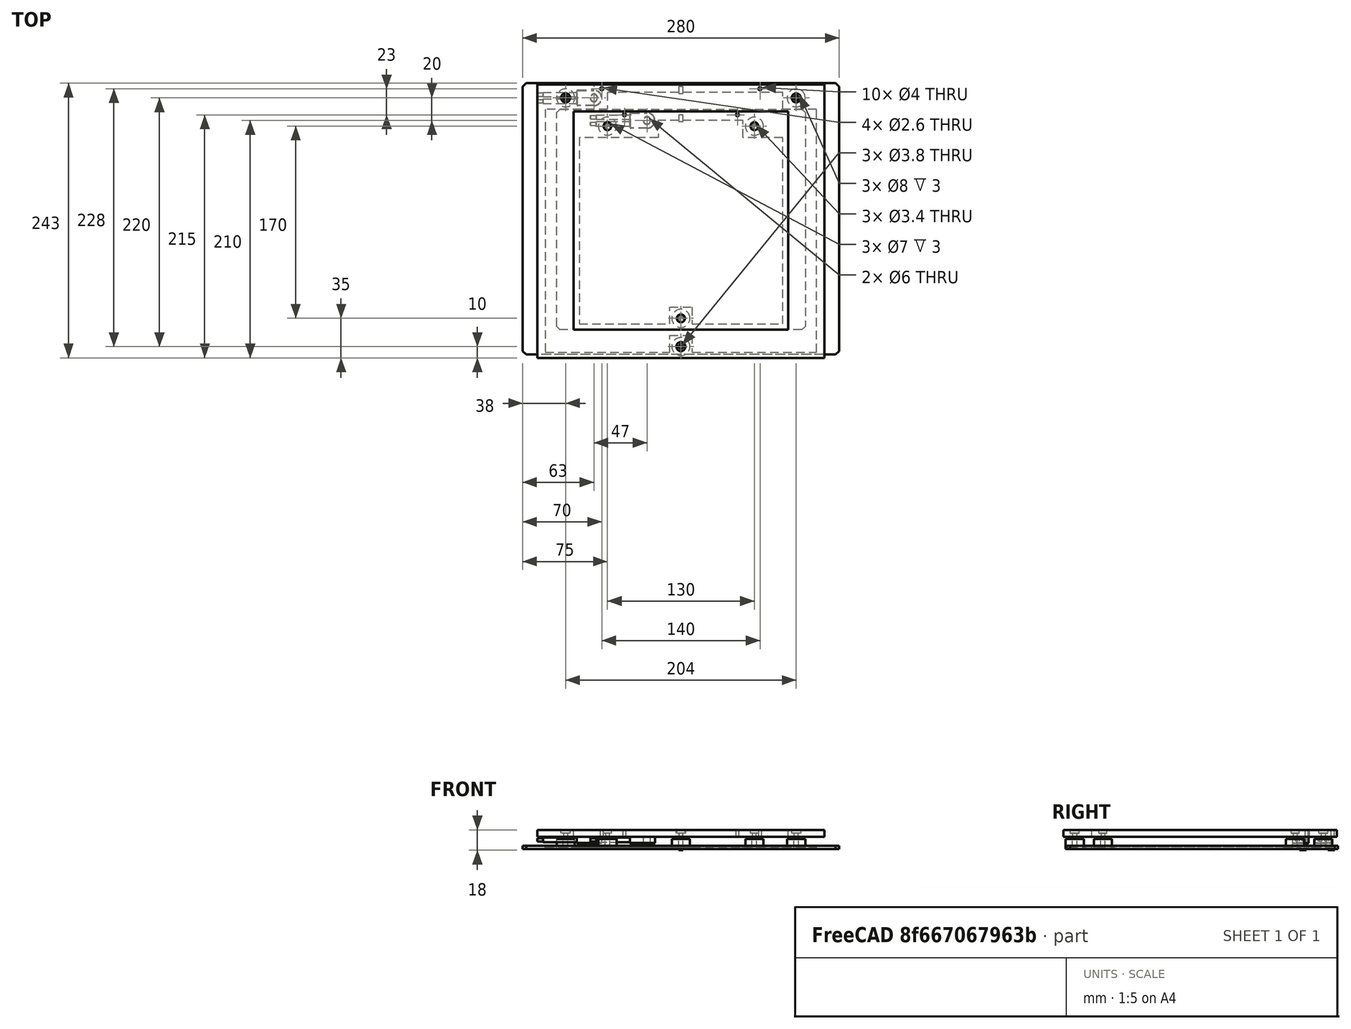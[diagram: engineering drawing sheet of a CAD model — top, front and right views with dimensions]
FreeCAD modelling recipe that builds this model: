
FCSTD DOCUMENT  (FreeCAD 0.19R24291 (Git))
Label: aluminum-bed
License: Other
LicenseURL: GPL3
objects: TechDraw::DrawViewDimension×50, Sketcher::SketchObject×10, TechDraw::DrawViewAnnotation×9, PartDesign::Pad×8, Part::Feature×8, PartDesign::Body×6, TechDraw::DrawSVGTemplate×5, TechDraw::DrawViewPart×5, TechDraw::DrawPage×5, TechDraw::DrawViewBalloon×3, PartDesign::Pocket×2, TechDraw::DrawViewSection×2, App::Part×2, PartDesign::Chamfer×2, TechDraw::DrawViewImage×1
note: 48 computed .brp shape members not serialized (recipe doc carries the construction recipe); baked Part::Feature solids carry a one-line shape summary decoded from their .brp

FEATURE [Sketcher::SketchObject] Sketch
  FullyConstrained = true
  MapMode = 5
  Support = -> [XY_Plane]
  sketch-geometry (9):
    g0: LineSegment StartX=-95 StartY=98 StartZ=0 EndX=95 EndY=98 EndZ=0
    g1: LineSegment StartX=95 StartY=98 StartZ=0 EndX=95 EndY=-95 EndZ=0
    g2: LineSegment StartX=95 StartY=-95 StartZ=0 EndX=-95 EndY=-95 EndZ=0
    g3: LineSegment StartX=-95 StartY=-95 StartZ=0 EndX=-95 EndY=98 EndZ=0
    g4: Circle CenterX=-1.4e-15 CenterY=-85 CenterZ=0 NormalX=0 NormalY=0 NormalZ=1 AngleXU=0 Radius=1.7
    g5: Circle CenterX=-65 CenterY=85 CenterZ=0 NormalX=0 NormalY=0 NormalZ=1 AngleXU=0 Radius=1.7
    g6: Circle CenterX=65 CenterY=85 CenterZ=0 NormalX=0 NormalY=0 NormalZ=1 AngleXU=0 Radius=1.7
    g7: Circle CenterX=-50 CenterY=95 CenterZ=0 NormalX=0 NormalY=0 NormalZ=1 AngleXU=0 Radius=1.3
    g8: Circle CenterX=50 CenterY=95 CenterZ=0 NormalX=0 NormalY=0 NormalZ=1 AngleXU=0 Radius=1.3
  constraints (27):
    c: Coincident(g0,g1)
    c: Coincident(g1,g2)
    c: Coincident(g2,g3)
    c: Coincident(g3,g0)
    c: Horizontal(g0)
    c: Horizontal(g2)
    c: Vertical(g1)
    c: Vertical(g3)
    c: DistanceY(g1,g1) = 193
    c: DistanceY(g2,g-1) = 95
    c: DistanceX(g0,g0) = 190
    c: DistanceX(g0,g-1) = 95
    c: DistanceX(g2,g4) = 95
    c: DistanceY(g1,g4) = 10
    c: DistanceY(g5,g0) = 13
    c: DistanceY(g6,g0) = 13
    c: DistanceX(g0,g5) = 30
    c: DistanceX(g6,g0) = 30
    c: Radius(g5) = 1.7
    c: Radius(g6) = 1.7
    c: Radius(g4) = 1.7
    c: DistanceX(g8,g0) = 45
    c: DistanceX(g0,g7) = 45
    c: Radius(g7) = 1.3
    c: Radius(g8) = 1.3
    c: DistanceY(g7,g0) = 3
    c: DistanceY(g8,g0) = 3
FEATURE [PartDesign::Pad] Pad
  Direction = (1,1,1)
  Length = 6
  Length2 = 100
  Profile = -> Sketch
  Type = 0
FEATURE [Sketcher::SketchObject] Sketch001
  FullyConstrained = true
  MapMode = 5
  Placement = pos=(0,0,6) rot=(0,0,1;0rad)
  Support = -> [Pad]
  sketch-geometry (3):
    g0: Circle CenterX=-65 CenterY=85 CenterZ=0 NormalX=0 NormalY=0 NormalZ=1 AngleXU=0 Radius=3.5
    g1: Circle CenterX=65 CenterY=85 CenterZ=0 NormalX=0 NormalY=0 NormalZ=1 AngleXU=0 Radius=3.5
    g2: Circle CenterX=0 CenterY=-85 CenterZ=0 NormalX=0 NormalY=0 NormalZ=1 AngleXU=0 Radius=3.5
  constraints (9):
    c: PointOnObject(g2,g-2)
    c: DistanceX(g0,g-1) = 65
    c: DistanceX(g-1,g1) = 65
    c: DistanceY(g2,g-1) = 85
    c: DistanceY(g-1,g0) = 85
    c: DistanceY(g-1,g1) = 85
    c: Radius(g0) = 3.5
    c: Radius(g1) = 3.5
    c: Radius(g2) = 3.5
FEATURE [PartDesign::Pocket] Pocket
  BaseFeature = -> Pad
  Length = 3
  Length2 = 100
  Profile = -> Sketch001
  Type = 0
FEATURE [PartDesign::Body] Body  label="190x193mm-bed"
  Group = -> [Sketch,Pad,Sketch001,Pocket]
  Origin = -> Origin
  Placement = pos=(0,0,11) rot=(0,0,1;0rad)
  Tip = -> Pocket
FEATURE [Sketcher::SketchObject] Sketch002
  FullyConstrained = true
  MapMode = 5
  Support = -> [XY_Plane001]
  sketch-geometry (9):
    g0: LineSegment StartX=-127 StartY=122 StartZ=0 EndX=127 EndY=122 EndZ=0
    g1: LineSegment StartX=127 StartY=122 StartZ=0 EndX=127 EndY=-120 EndZ=0
    g2: LineSegment StartX=127 StartY=-120 StartZ=0 EndX=-127 EndY=-120 EndZ=0
    g3: LineSegment StartX=-127 StartY=-120 StartZ=0 EndX=-127 EndY=122 EndZ=0
    g4: Circle CenterX=-102 CenterY=110 CenterZ=0 NormalX=0 NormalY=0 NormalZ=1 AngleXU=0 Radius=1.9
    g5: Circle CenterX=102 CenterY=110 CenterZ=0 NormalX=0 NormalY=0 NormalZ=1 AngleXU=0 Radius=1.9
    g6: Circle CenterX=0 CenterY=-110 CenterZ=0 NormalX=0 NormalY=0 NormalZ=1 AngleXU=0 Radius=1.9
    g7: Circle CenterX=-70 CenterY=118 CenterZ=0 NormalX=0 NormalY=0 NormalZ=1 AngleXU=0 Radius=1.3
    g8: Circle CenterX=70 CenterY=118 CenterZ=0 NormalX=0 NormalY=0 NormalZ=1 AngleXU=0 Radius=1.3
  constraints (27):
    c: Coincident(g0,g1)
    c: Coincident(g1,g2)
    c: Coincident(g2,g3)
    c: Coincident(g3,g0)
    c: Horizontal(g0)
    c: Horizontal(g2)
    c: Vertical(g1)
    c: Vertical(g3)
    c: DistanceX(g2,g2) = 254
    c: DistanceX(g2,g-1) = 127
    c: DistanceY(g3,g3) = 242
    c: DistanceY(g-1,g0) = 122
    c: DistanceX(g0,g4) = 25
    c: DistanceX(g5,g0) = 25
    c: DistanceY(g4,g0) = 12
    c: DistanceY(g5,g0) = 12
    c: DistanceY(g1,g6) = 10
    c: DistanceX(g6,g-1) = 0
    c: DistanceX(g7,g8) = 140
    c: DistanceX(g7,g-1) = 70
    c: DistanceY(g7,g8) = 0
    c: Radius(g7) = 1.3
    c: Radius(g8) = 1.3
    c: DistanceY(g7,g0) = 4
    c: Radius(g4) = 1.9
    c: Radius(g5) = 1.9
    c: Radius(g6) = 1.9
FEATURE [PartDesign::Pad] Pad001
  Direction = (1,1,1)
  Length = 6
  Length2 = 100
  Profile = -> Sketch002
  Type = 0
FEATURE [Sketcher::SketchObject] Sketch003
  FullyConstrained = true
  MapMode = 5
  Placement = pos=(0,0,6) rot=(0,0,1;0rad)
  Support = -> [Pad001]
  sketch-geometry (3):
    g0: Circle CenterX=-102 CenterY=110 CenterZ=0 NormalX=0 NormalY=0 NormalZ=1 AngleXU=0 Radius=4
    g1: Circle CenterX=102 CenterY=110 CenterZ=0 NormalX=0 NormalY=0 NormalZ=1 AngleXU=0 Radius=4
    g2: Circle CenterX=0 CenterY=-110 CenterZ=0 NormalX=0 NormalY=0 NormalZ=1 AngleXU=0 Radius=4
  constraints (9):
    c: PointOnObject(g2,g-2)
    c: Radius(g2) = 4
    c: Radius(g0) = 4
    c: Radius(g1) = 4
    c: DistanceY(g-1,g1) = 110
    c: DistanceX(g-1,g1) = 102
    c: DistanceX(g0,g-1) = 102
    c: DistanceY(g0,g1) = 0
    c: DistanceY(g2,g-1) = 110
FEATURE [PartDesign::Pocket] Pocket001
  BaseFeature = -> Pad001
  Length = 3
  Length2 = 100
  Profile = -> Sketch003
  Type = 0
FEATURE [PartDesign::Body] Body001  label="254x240-bed"
  Group = -> [Sketch002,Pad001,Sketch003,Pocket001]
  Origin = -> Origin001
  Placement = pos=(0,0,11) rot=(0,0,1;0rad)
  Tip = -> Pocket001
FEATURE [TechDraw::DrawSVGTemplate] Template
  EditableTexts = APPROVER_NAME=CB; AUTHOR_NAME=SnakeOil XY; DATE=2021-11-11; DN=DN; DOCUMENT_TYPE=Mechanical assembly drawing; OWNER_NAME=SnakeOil XY; PM=Silicon heater; PN=SO-180Heater; REVISION=REV B; RIGHTS=(R) DO NOT DUPLICATE THIS DRAWING TO THIRD PARTIES WITHOUT OWNER'S PERMISSION!; SCALE=1.0; SHEET=99 of 99; SIZE=A3; TITLELINE-1=SnakeOil XY; TITLELINE-2=180x180mm Silicon heater 120V 350-400W; TITLELINE-3=Dimensions in mm; TOLERANCE=+/- 0.2mm
  Height = 297
  Orientation = 1
  Width = 420
FEATURE [TechDraw::DrawSVGTemplate] Template002
  EditableTexts = APPROVER_NAME=CB; AUTHOR_NAME=SnakeOil XY; DATE=2021-11-09; DN=DN; DOCUMENT_TYPE=Mechanical assembly drawing; OWNER_NAME=SnakeOil XY; PM=Aluminum 6mm Plate; PN=SO-250Bed; REVISION=REV A; RIGHTS=(R) DO NOT DUPLICATE THIS DRAWING TO THIRD PARTIES WITHOUT OWNER'S PERMISSION!; SCALE=0.75; SHEET=99 of 99; SIZE=A3; TITLELINE-1=SnakeOil XY; TITLELINE-2=242x254mm Aluminium Bed; TITLELINE-3=Dimensions in mm; TOLERANCE=+/- 0.2mm
  Height = 297
  Orientation = 1
  Width = 420
FEATURE [TechDraw::DrawViewPart] View002  label="Top View"
  CoarseView = false
  Direction = (0,0,1)
  Focus = 100
  HardHidden = true
  IsoCount = 0
  IsoHidden = true
  IsoVisible = false
  LockPosition = false
  Perspective = false
  Rotation = 0
  Scale = 0.75
  ScaleType = 0
  SeamHidden = true
  SeamVisible = true
  SmoothHidden = false
  SmoothVisible = true
  Source = -> [Body001]
  X = 187.091
  XDirection = (1,0,0)
  Y = 157.532
FEATURE [TechDraw::DrawViewDimension] Dimension008
  Arbitrary = false
  ArbitraryTolerances = false
  EqualTolerance = true
  FormatSpec = %.2f
  FormatSpecOverTolerance = %+.2f
  FormatSpecUnderTolerance = %+.2f
  Inverted = false
  LockPosition = false
  MeasureType = 1
  OverTolerance = 0
  References2D = -> [View002]
  Rotation = 0
  ScaleType = 0
  TheoreticalExact = false
  Type = 2
  UnderTolerance = 0
  X = -129.591
  Y = 4.6265
FEATURE [TechDraw::DrawViewDimension] Dimension009
  Arbitrary = false
  ArbitraryTolerances = false
  EqualTolerance = true
  FormatSpec = %.2f
  FormatSpecOverTolerance = %+.2f
  FormatSpecUnderTolerance = %+.2f
  Inverted = false
  LockPosition = false
  MeasureType = 1
  OverTolerance = 0
  References2D = -> [View002]
  Rotation = 0
  ScaleType = 0
  TheoreticalExact = false
  Type = 1
  UnderTolerance = 0
  X = -3.77464
  Y = 114.946
FEATURE [TechDraw::DrawViewDimension] Dimension010
  Arbitrary = false
  ArbitraryTolerances = false
  EqualTolerance = true
  FormatSpec = %.2f
  FormatSpecOverTolerance = %+.2f
  FormatSpecUnderTolerance = %+.2f
  Inverted = false
  LockPosition = false
  MeasureType = 1
  OverTolerance = 0
  References2D = -> [View002]
  Rotation = 0
  ScaleType = 0
  TheoreticalExact = false
  Type = 1
  UnderTolerance = 0
  X = -85.9693
  Y = 105.298
FEATURE [TechDraw::DrawViewDimension] Dimension018
  Arbitrary = false
  ArbitraryTolerances = false
  EqualTolerance = true
  FormatSpec = %.2f
  FormatSpecOverTolerance = %+.2f
  FormatSpecUnderTolerance = %+.2f
  Inverted = false
  LockPosition = false
  MeasureType = 1
  OverTolerance = 0
  References2D = -> [View002]
  Rotation = 0
  ScaleType = 0
  TheoreticalExact = false
  Type = 1
  UnderTolerance = 0
  X = -48.5489
  Y = -96.978
FEATURE [TechDraw::DrawViewDimension] Dimension019
  Arbitrary = false
  ArbitraryTolerances = false
  EqualTolerance = true
  FormatSpec = %.2f
  FormatSpecOverTolerance = %+.2f
  FormatSpecUnderTolerance = %+.2f
  Inverted = false
  LockPosition = false
  MeasureType = 1
  OverTolerance = 0
  References2D = -> [View002]
  Rotation = 0
  ScaleType = 0
  TheoreticalExact = false
  Type = 2
  UnderTolerance = 0
  X = -107.541
  Y = -67.6889
FEATURE [TechDraw::DrawViewDimension] Dimension024
  Arbitrary = false
  ArbitraryTolerances = false
  EqualTolerance = true
  FormatSpec = 3x ⌀%.2f THRU ALL
  FormatSpecOverTolerance = %+.2f
  FormatSpecUnderTolerance = %+.2f
  Inverted = false
  LockPosition = false
  MeasureType = 1
  OverTolerance = 0
  References2D = -> [View002]
  Rotation = 0
  ScaleType = 0
  TheoreticalExact = false
  Type = 5
  UnderTolerance = 0
  X = 28.5305
  Y = -62.0287
FEATURE [TechDraw::DrawViewDimension] Dimension011
  Arbitrary = false
  ArbitraryTolerances = false
  EqualTolerance = true
  FormatSpec = %.2f
  FormatSpecOverTolerance = %+.2f
  FormatSpecUnderTolerance = %+.2f
  Inverted = false
  LockPosition = false
  MeasureType = 1
  OverTolerance = 0
  References2D = -> [View002]
  Rotation = 0
  ScaleType = 0
  TheoreticalExact = false
  Type = 1
  UnderTolerance = 0
  X = -64.1413
  Y = 105.194
FEATURE [TechDraw::DrawViewDimension] Dimension028
  Arbitrary = false
  ArbitraryTolerances = false
  EqualTolerance = true
  FormatSpec = %.2f
  FormatSpecOverTolerance = %+.2f
  FormatSpecUnderTolerance = %+.2f
  Inverted = false
  LockPosition = false
  MeasureType = 1
  OverTolerance = 0
  References2D = -> [View002]
  Rotation = 0
  ScaleType = 0
  TheoreticalExact = false
  Type = 2
  UnderTolerance = 0
  X = -108.367
  Y = 69.0185
FEATURE [TechDraw::DrawViewSection] SectionView  label="Section A - A"
  BaseView = -> View002
  CoarseView = false
  CutSurfaceDisplay = 2
  Direction = (1,0,0)
  FileGeomPattern = C:/Program Files/FreeCAD 0.19/data/Mod/TechDraw/PAT/FCPAT.pat
  FileHatchPattern = C:/Program Files/FreeCAD 0.19/data/Mod/TechDraw/Patterns/simple.svg
  Focus = 100
  FuseBeforeCut = false
  HardHidden = true
  HatchScale = 1
  IsoCount = 0
  IsoHidden = false
  IsoVisible = false
  LockPosition = false
  NameGeomPattern = Diamond
  Perspective = false
  Rotation = 0
  Scale = 0.75
  ScaleType = 0
  SeamHidden = false
  SeamVisible = true
  SectionDirection = 1
  SectionNormal = (1,0,0)
  SectionOrigin = (0,1,-20)
  SectionSymbol = A
  SmoothHidden = false
  SmoothVisible = true
  Source = -> [Body001]
  X = 361.828
  XDirection = (0,0,-1)
  Y = 157.254
FEATURE [TechDraw::DrawViewDimension] Dimension030
  Arbitrary = false
  ArbitraryTolerances = false
  EqualTolerance = true
  FormatSpec = %.2f
  FormatSpecOverTolerance = %+.2f
  FormatSpecUnderTolerance = %+.2f
  Inverted = false
  LockPosition = false
  MeasureType = 1
  OverTolerance = 0
  References2D = -> [SectionView]
  Rotation = 0
  ScaleType = 0
  TheoreticalExact = false
  Type = 2
  UnderTolerance = 0
  X = -21.0566
  Y = -66.6227
FEATURE [TechDraw::DrawViewDimension] Dimension031
  Arbitrary = false
  ArbitraryTolerances = false
  EqualTolerance = true
  FormatSpec = %.2f
  FormatSpecOverTolerance = %+.2f
  FormatSpecUnderTolerance = %+.2f
  Inverted = false
  LockPosition = false
  MeasureType = 1
  OverTolerance = 0
  References2D = -> [SectionView]
  Rotation = 0
  ScaleType = 0
  TheoreticalExact = false
  Type = 0
  UnderTolerance = 0
  X = 11.4648
  Y = -70.64
FEATURE [TechDraw::DrawViewDimension] Dimension032
  Arbitrary = false
  ArbitraryTolerances = false
  EqualTolerance = true
  FormatSpec = %.2f
  FormatSpecOverTolerance = %+.2f
  FormatSpecUnderTolerance = %+.2f
  Inverted = false
  LockPosition = false
  MeasureType = 1
  OverTolerance = 0
  References2D = -> [SectionView]
  Rotation = 0
  ScaleType = 0
  TheoreticalExact = false
  Type = 0
  UnderTolerance = 0
  X = -2.15303
  Y = 102.385
FEATURE [TechDraw::DrawViewDimension] Dimension033
  Arbitrary = false
  ArbitraryTolerances = false
  EqualTolerance = true
  FormatSpec = %.2f
  FormatSpecOverTolerance = %+.2f
  FormatSpecUnderTolerance = %+.2f
  Inverted = false
  LockPosition = false
  MeasureType = 1
  OverTolerance = 0
  References2D = -> [View002]
  Rotation = 0
  ScaleType = 0
  TheoreticalExact = false
  Type = 2
  UnderTolerance = 0
  X = -117.954
  Y = 68.1477
FEATURE [TechDraw::DrawViewDimension] Dimension034
  Arbitrary = false
  ArbitraryTolerances = false
  EqualTolerance = true
  FormatSpec = 2x ⌀%.2f THRU ALL
  FormatSpecOverTolerance = %+.2f
  FormatSpecUnderTolerance = %+.2f
  Inverted = false
  LockPosition = false
  MeasureType = 1
  OverTolerance = 0
  References2D = -> [View002]
  Rotation = 0
  ScaleType = 0
  TheoreticalExact = false
  Type = 5
  UnderTolerance = 0
  X = 26.933
  Y = 78.1529
FEATURE [TechDraw::DrawViewImage] Image
  Height = 25
  ImageFile = <userpath>/Desktop/SnakeOil Logo Banner.png
  LockPosition = false
  Rotation = 0
  Scale = 0.12
  ScaleType = 2
  Width = 25
  X = 332.066
  Y = 27.4423
FEATURE [TechDraw::DrawViewAnnotation] Annotation
  Font = Open Sans
  LineSpace = 80
  LockPosition = false
  MaxWidth = -1
  Rotation = 0
  ScaleType = 0
  Text =  \u2334 \u23008.00 \u21a7 3.00
  TextSize = 5
  TextStyle = 0
  X = 211.577
  Y = 85.7344
FEATURE [TechDraw::DrawViewAnnotation] Annotation001
  Font = Open Sans
  LineSpace = 80
  LockPosition = false
  MaxWidth = -1
  Rotation = 0
  ScaleType = 0
  Text = M3 THRU ALL
  TextSize = 5
  TextStyle = 0
  X = 207.027
  Y = 225.227
FEATURE [TechDraw::DrawPage] Page002  label="250-aluminum-bed"
  KeepUpdated = true
  NextBalloonIndex = 3
  ProjectionType = 0
  Template = -> Template002
  Views = -> [View002,Dimension008,Dimension009,Dimension010,Dimension011,Dimension018,Dimension019,Dimension024,Dimension028,SectionView,Dimension030,Dimension031,Dimension032,Dimension033,Dimension034,Image,Annotation,Annotation001]
FEATURE [TechDraw::DrawSVGTemplate] Template003
  EditableTexts = APPROVER_NAME=CB; AUTHOR_NAME=SnakeOil XY; DATE=2021-11-09; DN=DN; DOCUMENT_TYPE=Mechanical assembly drawing; OWNER_NAME=SnakeOil XY; PM=Aluminum 6mm Plate; PN=SO-180Bed; REVISION=REV A; RIGHTS=(R) DO NOT DUPLICATE THIS DRAWING TO THIRD PARTIES WITHOUT OWNER'S PERMISSION!; SCALE=1.0; SHEET=99 of 99; SIZE=A3; TITLELINE-1=SnakeOil XY; TITLELINE-2=190x193mm Aluminium Bed; TITLELINE-3=Dimensions in mm; TOLERANCE=+/- 0.2mm
  Height = 297
  Orientation = 1
  Width = 420
FEATURE [TechDraw::DrawViewPart] View003
  CoarseView = false
  Direction = (0,0,1)
  Focus = 100
  HardHidden = true
  IsoCount = 0
  IsoHidden = true
  IsoVisible = false
  LockPosition = false
  Perspective = false
  Rotation = 0
  ScaleType = 0
  SeamHidden = true
  SeamVisible = true
  SmoothHidden = false
  SmoothVisible = true
  Source = -> [Body]
  X = 163.077
  XDirection = (1,0,0)
  Y = 159.843
FEATURE [TechDraw::DrawViewDimension] Dimension062
  Arbitrary = false
  ArbitraryTolerances = false
  EqualTolerance = true
  FormatSpec = %.2f
  FormatSpecOverTolerance = %+.2f
  FormatSpecUnderTolerance = %+.2f
  Inverted = false
  LockPosition = false
  MeasureType = 1
  OverTolerance = 0
  References2D = -> [View003]
  Rotation = 0
  ScaleType = 0
  TheoreticalExact = false
  Type = 2
  UnderTolerance = 0
  X = -125.383
  Y = 2.51695
FEATURE [TechDraw::DrawViewDimension] Dimension063
  Arbitrary = false
  ArbitraryTolerances = false
  EqualTolerance = true
  FormatSpec = %.2f
  FormatSpecOverTolerance = %+.2f
  FormatSpecUnderTolerance = %+.2f
  Inverted = false
  LockPosition = false
  MeasureType = 1
  OverTolerance = 0
  References2D = -> [View003]
  Rotation = 0
  ScaleType = 0
  TheoreticalExact = false
  Type = 2
  UnderTolerance = 0
  X = -116.496
  Y = 75.6174
FEATURE [TechDraw::DrawViewDimension] Dimension064
  Arbitrary = false
  ArbitraryTolerances = false
  EqualTolerance = true
  FormatSpec = %.2f
  FormatSpecOverTolerance = %+.2f
  FormatSpecUnderTolerance = %+.2f
  Inverted = false
  LockPosition = false
  MeasureType = 1
  OverTolerance = 0
  References2D = -> [View003]
  Rotation = 0
  ScaleType = 0
  TheoreticalExact = false
  Type = 2
  UnderTolerance = 0
  X = -107.25
  Y = 74.8161
FEATURE [TechDraw::DrawViewDimension] Dimension066
  Arbitrary = false
  ArbitraryTolerances = false
  EqualTolerance = true
  FormatSpec = %.2f
  FormatSpecOverTolerance = %+.2f
  FormatSpecUnderTolerance = %+.2f
  Inverted = false
  LockPosition = false
  MeasureType = 1
  OverTolerance = 0
  References2D = -> [View003]
  Rotation = 0
  ScaleType = 0
  TheoreticalExact = false
  Type = 1
  UnderTolerance = 0
  X = -47.3359
  Y = -97.9006
FEATURE [TechDraw::DrawViewDimension] Dimension067
  Arbitrary = false
  ArbitraryTolerances = false
  EqualTolerance = true
  FormatSpec = %.2f
  FormatSpecOverTolerance = %+.2f
  FormatSpecUnderTolerance = %+.2f
  Inverted = false
  LockPosition = false
  MeasureType = 1
  OverTolerance = 0
  References2D = -> [View003]
  Rotation = 0
  ScaleType = 0
  TheoreticalExact = false
  Type = 1
  UnderTolerance = 0
  X = -1.8053
  Y = 121.118
FEATURE [TechDraw::DrawViewDimension] Dimension068
  Arbitrary = false
  ArbitraryTolerances = false
  EqualTolerance = true
  FormatSpec = %.2f
  FormatSpecOverTolerance = %+.2f
  FormatSpecUnderTolerance = %+.2f
  Inverted = false
  LockPosition = false
  MeasureType = 1
  OverTolerance = 0
  References2D = -> [View003]
  Rotation = 0
  ScaleType = 0
  TheoreticalExact = false
  Type = 1
  UnderTolerance = 0
  X = -81.0404
  Y = 110.461
FEATURE [TechDraw::DrawViewDimension] Dimension069
  Arbitrary = false
  ArbitraryTolerances = false
  EqualTolerance = true
  FormatSpec = %.2f
  FormatSpecOverTolerance = %+.2f
  FormatSpecUnderTolerance = %+.2f
  Inverted = false
  LockPosition = false
  MeasureType = 1
  OverTolerance = 0
  References2D = -> [View003]
  Rotation = 0
  ScaleType = 0
  TheoreticalExact = false
  Type = 1
  UnderTolerance = 0
  X = -57.9335
  Y = 110.522
FEATURE [TechDraw::DrawViewDimension] Dimension070
  Arbitrary = false
  ArbitraryTolerances = false
  EqualTolerance = true
  FormatSpec = 2x ⌀%.2f THRU ALL
  FormatSpecOverTolerance = %+.2f
  FormatSpecUnderTolerance = %+.2f
  Inverted = false
  LockPosition = false
  MeasureType = 1
  OverTolerance = 0
  References2D = -> [View003]
  Rotation = 0
  ScaleType = 0
  TheoreticalExact = false
  Type = 5
  UnderTolerance = 0
  X = 23.3527
  Y = 89.8776
FEATURE [TechDraw::DrawViewDimension] Dimension071
  Arbitrary = false
  ArbitraryTolerances = false
  EqualTolerance = true
  FormatSpec = 3x ⌀%.2f THRU ALL
  FormatSpecOverTolerance = %+.2f
  FormatSpecUnderTolerance = %+.2f
  Inverted = false
  LockPosition = false
  MeasureType = 1
  OverTolerance = 0
  References2D = -> [View003]
  Rotation = 0
  ScaleType = 0
  TheoreticalExact = false
  Type = 5
  UnderTolerance = 0
  X = 33.3476
  Y = -62.6573
FEATURE [TechDraw::DrawViewAnnotation] Annotation002
  Font = osifont
  LineSpace = 80
  LockPosition = false
  MaxWidth = -1
  Rotation = 0
  ScaleType = 0
  Text = M3 THRU ALL
  TextSize = 5
  TextStyle = 0
  X = 180.845
  Y = 237.091
FEATURE [TechDraw::DrawViewAnnotation] Annotation003
  Font = osifont
  LineSpace = 80
  LockPosition = false
  MaxWidth = -1
  Rotation = 0
  ScaleType = 0
  Text =  \u2334 \u23007.00 \u21a7 3.00
  TextSize = 5
  TextStyle = 0
  X = 198.079
  Y = 84.8751
FEATURE [TechDraw::DrawViewSection] SectionView001  label="Section A - A001"
  BaseView = -> View003
  CoarseView = false
  CutSurfaceDisplay = 2
  Direction = (1,0,0)
  FileGeomPattern = <path>
  FileHatchPattern = <path>
  Focus = 100
  FuseBeforeCut = false
  HardHidden = false
  HatchScale = 1
  IsoCount = 0
  IsoHidden = false
  IsoVisible = false
  LockPosition = false
  NameGeomPattern = Diamond
  Perspective = false
  Rotation = 0
  ScaleType = 0
  SeamHidden = false
  SeamVisible = true
  SectionDirection = 1
  SectionNormal = (1,0,0)
  SectionOrigin = (0,1.5,-43)
  SectionSymbol = A
  SmoothHidden = false
  SmoothVisible = true
  Source = -> [Body]
  X = 321.285
  XDirection = (0,0,-1)
  Y = 159.826
FEATURE [TechDraw::DrawViewDimension] Dimension072
  Arbitrary = false
  ArbitraryTolerances = false
  EqualTolerance = true
  FormatSpec = %.2f
  FormatSpecOverTolerance = %+.2f
  FormatSpecUnderTolerance = %+.2f
  Inverted = false
  LockPosition = false
  MeasureType = 1
  OverTolerance = 0
  References2D = -> [SectionView001]
  Rotation = 0
  ScaleType = 0
  TheoreticalExact = false
  Type = 1
  UnderTolerance = 0
  X = -0.208081
  Y = 106.28
FEATURE [TechDraw::DrawViewDimension] Dimension073
  Arbitrary = false
  ArbitraryTolerances = false
  EqualTolerance = true
  FormatSpec = %.2f
  FormatSpecOverTolerance = %+.2f
  FormatSpecUnderTolerance = %+.2f
  Inverted = false
  LockPosition = false
  MeasureType = 1
  OverTolerance = 0
  References2D = -> [SectionView001]
  Rotation = 0
  ScaleType = 0
  TheoreticalExact = false
  Type = 2
  UnderTolerance = 0
  X = -20.3682
  Y = -75.6723
FEATURE [TechDraw::DrawViewDimension] Dimension074
  Arbitrary = false
  ArbitraryTolerances = false
  EqualTolerance = true
  FormatSpec = %.2f
  FormatSpecOverTolerance = %+.2f
  FormatSpecUnderTolerance = %+.2f
  Inverted = false
  LockPosition = false
  MeasureType = 1
  OverTolerance = 0
  References2D = -> [SectionView001]
  Rotation = 0
  ScaleType = 0
  TheoreticalExact = false
  Type = 1
  UnderTolerance = 0
  X = 9.43758
  Y = -71.1281
FEATURE [TechDraw::DrawViewDimension] Dimension075
  Arbitrary = false
  ArbitraryTolerances = false
  EqualTolerance = true
  FormatSpec = %.2f
  FormatSpecOverTolerance = %+.2f
  FormatSpecUnderTolerance = %+.2f
  Inverted = false
  LockPosition = false
  MeasureType = 1
  OverTolerance = 0
  References2D = -> [View003]
  Rotation = 0
  ScaleType = 0
  TheoreticalExact = false
  Type = 2
  UnderTolerance = 0
  X = -111.672
  Y = -73.2721
FEATURE [TechDraw::DrawPage] Page003  label="180-aluminum-bed"
  KeepUpdated = true
  NextBalloonIndex = 1
  ProjectionType = 0
  Template = -> Template003
  Views = -> [View003,Dimension062,Dimension063,Dimension064,Dimension066,Dimension067,Dimension068,Dimension069,Dimension070,Dimension071,Annotation002,Annotation003,SectionView001,Dimension072,Dimension073,Dimension074,Dimension075]
FEATURE [Part::Feature] Part__Feature003  label="thermal-fuse-180"
  Placement = pos=(-30,90,11.18) rot=(0,1,0;1.5708rad)
  shape: bbox 57 x 14 x 6 mm, 31 faces (baked)
FEATURE [Part::Feature] Cut001  label="silicon-spacer"
  Placement = pos=(65,85,0) rot=(0,0,1;0rad)
  shape: bbox 16 x 16 x 9 mm, 4 faces (baked)
FEATURE [Part::Feature] Cut002  label="silicon-spacer001"
  Placement = pos=(-65,85,0) rot=(0,0,1;0rad)
  shape: bbox 16 x 16 x 9 mm, 4 faces (baked)
FEATURE [Part::Feature] Cut003  label="silicon-spacer002"
  Placement = pos=(0,-85,0) rot=(0,0,1;0rad)
  shape: bbox 16 x 16 x 9 mm, 4 faces (baked)
FEATURE [App::Part] Part  label="180-bed-assembly"
  Group = -> [Part__Feature003,Cut001,Cut002,Cut003,Body]
  Origin = -> Origin004
  Placement = pos=(0,0,-20) rot=(0,0,1;0rad)
FEATURE [Sketcher::SketchObject] Sketch009
  FullyConstrained = true
  MapMode = 5
  Support = -> [XY_Plane002]
  sketch-geometry (12):
    g0: LineSegment StartX=-90 StartY=75 StartZ=0 EndX=-90 EndY=-90 EndZ=0
    g1: LineSegment StartX=-90 StartY=-90 StartZ=0 EndX=-10 EndY=-90 EndZ=0
    g2: LineSegment StartX=-10 StartY=-90 StartZ=0 EndX=-10 EndY=-75 EndZ=0
    g3: LineSegment StartX=-10 StartY=-75 StartZ=0 EndX=10 EndY=-75 EndZ=0
    g4: LineSegment StartX=10 StartY=-75 StartZ=0 EndX=10 EndY=-90 EndZ=0
    g5: LineSegment StartX=10 StartY=-90 StartZ=0 EndX=90 EndY=-90 EndZ=0
    g6: LineSegment StartX=90 StartY=-90 StartZ=0 EndX=90 EndY=75 EndZ=0
    g7: LineSegment StartX=90 StartY=75 StartZ=0 EndX=55 EndY=75 EndZ=0
    g8: LineSegment StartX=55 StartY=75 StartZ=0 EndX=55 EndY=90 EndZ=0
    g9: LineSegment StartX=55 StartY=90 StartZ=0 EndX=-20 EndY=90 EndZ=0
    g10: LineSegment StartX=-20 StartY=90 StartZ=0 EndX=-20 EndY=75 EndZ=0
    g11: LineSegment StartX=-20 StartY=75 StartZ=0 EndX=-90 EndY=75 EndZ=0
  constraints (36):
    c: Vertical(g0)
    c: Coincident(g0,g1)
    c: Horizontal(g1)
    c: Coincident(g1,g2)
    c: Vertical(g2)
    c: Coincident(g2,g3)
    c: Horizontal(g3)
    c: Coincident(g3,g4)
    c: Vertical(g4)
    c: Coincident(g4,g5)
    c: Horizontal(g5)
    c: Coincident(g5,g6)
    c: Vertical(g6)
    c: Coincident(g6,g7)
    c: Horizontal(g7)
    c: Coincident(g7,g8)
    c: Vertical(g8)
    c: Coincident(g8,g9)
    c: Horizontal(g9)
    c: Coincident(g9,g10)
    c: Vertical(g10)
    c: Coincident(g10,g11)
    c: Coincident(g11,g0)
    c: Horizontal(g11)
    c: DistanceX(g0,g5) = 180
    c: DistanceX(g1,g4) = 20
    c: DistanceX(g2,g-1) = 10
    c: DistanceX(g0,g-1) = 90
    c: DistanceY(g3,g-1) = 75
    c: DistanceY(g-1,g0) = 75
    c: DistanceY(g-1,g6) = 75
    c: DistanceX(g10,g-1) = 20
    c: DistanceX(g-1,g7) = 55
    c: DistanceY(g-1,g8) = 90
    c: DistanceY(g0,g0) = 165
    c: DistanceY(g4,g4) = 15
FEATURE [PartDesign::Pad] Pad007
  Direction = (1,1,1)
  Length = 2
  Length2 = 100
  Profile = -> Sketch009
  Type = 0
FEATURE [Sketcher::SketchObject] Sketch010
  FullyConstrained = false
  MapMode = 5
  Placement = pos=(0,0,2) rot=(0,0,1;0rad)
  Support = -> [Pad007]
  sketch-geometry (4):
    g0: LineSegment StartX=-2 StartY=89 StartZ=0 EndX=2 EndY=89 EndZ=0
    g1: LineSegment StartX=2 StartY=89 StartZ=0 EndX=2 EndY=95 EndZ=0
    g2: LineSegment StartX=2 StartY=95 StartZ=0 EndX=-2 EndY=95 EndZ=0
    g3: LineSegment StartX=-2 StartY=95 StartZ=0 EndX=-2 EndY=89 EndZ=0
  constraints (8):
    c: Coincident(g0,g1)
    c: Coincident(g1,g2)
    c: Coincident(g2,g3)
    c: Coincident(g3,g0)
    c: Horizontal(g0)
    c: Horizontal(g2)
    c: Vertical(g1)
    c: Vertical(g3)
FEATURE [PartDesign::Pad] Pad008
  BaseFeature = -> Pad007
  Direction = (1,1,1)
  Length = 3
  Length2 = 100
  Profile = -> Sketch010
  Reversed = true
  Type = 0
FEATURE [PartDesign::Body] Body002  label="180-heater"
  Group = -> [Sketch009,Pad007,Sketch010,Pad008]
  Origin = -> Origin002
  Tip = -> Pad008
FEATURE [Part::Feature] Cut004  label="silicon-spacer003"
  Placement = pos=(0,-110,0) rot=(0,0,1;0rad)
  shape: bbox 16 x 16 x 9 mm, 4 faces (baked)
FEATURE [Part::Feature] Cut005  label="silicon-spacer004"
  Placement = pos=(102,110,0) rot=(0,0,1;0rad)
  shape: bbox 16 x 16 x 9 mm, 4 faces (baked)
FEATURE [Part::Feature] Cut006  label="silicon-spacer005"
  Placement = pos=(-102,110,0) rot=(0,0,1;0rad)
  shape: bbox 16 x 16 x 9 mm, 4 faces (baked)
FEATURE [Part::Feature] Part__Feature004  label="thermal-fuse-181"
  Placement = pos=(-77,110,11.18) rot=(0,1,0;1.5708rad)
  shape: bbox 57 x 14 x 6 mm, 31 faces (baked)
FEATURE [App::Part] Part001  label="250-bed-assembly"
  Group = -> [Cut004,Cut005,Cut006,Part__Feature004,Body001]
  Origin = -> Origin005
  Placement = pos=(0,0,-39) rot=(0,0,1;0rad)
FEATURE [Sketcher::SketchObject] Sketch011
  FullyConstrained = true
  MapMode = 5
  Support = -> [XY_Plane003]
  sketch-geometry (12):
    g0: LineSegment StartX=-120 StartY=100 StartZ=0 EndX=-120 EndY=-115 EndZ=0
    g1: LineSegment StartX=-120 StartY=-115 StartZ=0 EndX=-10 EndY=-115 EndZ=0
    g2: LineSegment StartX=-10 StartY=-115 StartZ=0 EndX=-10 EndY=-100 EndZ=0
    g3: LineSegment StartX=-10 StartY=-100 StartZ=0 EndX=10 EndY=-100 EndZ=0
    g4: LineSegment StartX=10 StartY=-100 StartZ=0 EndX=10 EndY=-115 EndZ=0
    g5: LineSegment StartX=10 StartY=-115 StartZ=0 EndX=120 EndY=-115 EndZ=0
    g6: LineSegment StartX=120 StartY=-115 StartZ=0 EndX=120 EndY=100 EndZ=0
    g7: LineSegment StartX=120 StartY=100 StartZ=0 EndX=90 EndY=100 EndZ=0
    g8: LineSegment StartX=90 StartY=100 StartZ=0 EndX=90 EndY=115 EndZ=0
    g9: LineSegment StartX=90 StartY=115 StartZ=0 EndX=-65 EndY=115 EndZ=0
    g10: LineSegment StartX=-65 StartY=115 StartZ=0 EndX=-65 EndY=100 EndZ=0
    g11: LineSegment StartX=-65 StartY=100 StartZ=0 EndX=-120 EndY=100 EndZ=0
  constraints (36):
    c: Vertical(g0)
    c: Coincident(g0,g1)
    c: Horizontal(g1)
    c: Coincident(g1,g2)
    c: Vertical(g2)
    c: Coincident(g2,g3)
    c: Horizontal(g3)
    c: Coincident(g3,g4)
    c: Vertical(g4)
    c: Coincident(g4,g5)
    c: Horizontal(g5)
    c: Coincident(g5,g6)
    c: Vertical(g6)
    c: Coincident(g6,g7)
    c: Horizontal(g7)
    c: Coincident(g7,g8)
    c: Vertical(g8)
    c: Coincident(g8,g9)
    c: Horizontal(g9)
    c: Coincident(g9,g10)
    c: Vertical(g10)
    c: Coincident(g10,g11)
    c: Coincident(g11,g0)
    c: Horizontal(g11)
    c: DistanceY(g2,g2) = 15
    c: DistanceY(g4,g4) = 15
    c: DistanceX(g3,g3) = 20
    c: DistanceX(g0,g-1) = 120
    c: DistanceX(g0,g5) = 240
    c: DistanceY(g0,g-1) = 115
    c: DistanceX(g2,g-1) = 10
    c: DistanceY(g-1,g0) = 100
    c: DistanceY(g-1,g6) = 100
    c: DistanceX(g-1,g7) = 90
    c: DistanceY(g-1,g8) = 115
    c: DistanceX(g9,g-1) = 65
FEATURE [PartDesign::Pad] Pad009
  Direction = (1,1,1)
  Length = 2
  Length2 = 100
  Profile = -> Sketch011
  Type = 0
FEATURE [Sketcher::SketchObject] Sketch012
  FullyConstrained = false
  MapMode = 5
  Placement = pos=(0,0,2) rot=(0,0,1;0rad)
  Support = -> [Pad009]
  sketch-geometry (4):
    g0: LineSegment StartX=-2 StartY=114 StartZ=0 EndX=2 EndY=114 EndZ=0
    g1: LineSegment StartX=2 StartY=114 StartZ=0 EndX=2 EndY=120 EndZ=0
    g2: LineSegment StartX=2 StartY=120 StartZ=0 EndX=-2 EndY=120 EndZ=0
    g3: LineSegment StartX=-2 StartY=120 StartZ=0 EndX=-2 EndY=114 EndZ=0
  constraints (8):
    c: Coincident(g0,g1)
    c: Coincident(g1,g2)
    c: Coincident(g2,g3)
    c: Coincident(g3,g0)
    c: Horizontal(g0)
    c: Horizontal(g2)
    c: Vertical(g1)
    c: Vertical(g3)
FEATURE [PartDesign::Pad] Pad010
  BaseFeature = -> Pad009
  Direction = (1,1,1)
  Length = 3
  Length2 = 100
  Profile = -> Sketch012
  Reversed = true
  Type = 0
FEATURE [PartDesign::Body] Body003  label="250-heater"
  Group = -> [Sketch011,Pad009,Sketch012,Pad010]
  Origin = -> Origin003
  Tip = -> Pad010
FEATURE [TechDraw::DrawViewPart] View
  CoarseView = false
  Direction = (0,0,1)
  Focus = 100
  HardHidden = false
  IsoCount = 0
  IsoHidden = false
  IsoVisible = false
  LockPosition = false
  Perspective = false
  Rotation = 0
  ScaleType = 0
  SeamHidden = false
  SeamVisible = true
  SmoothHidden = false
  SmoothVisible = true
  Source = -> [Body002]
  X = 156.162
  XDirection = (1,0,0)
  Y = 160.088
FEATURE [TechDraw::DrawViewDimension] Dimension
  Arbitrary = false
  ArbitraryTolerances = false
  EqualTolerance = true
  FormatSpec = %.2f
  FormatSpecOverTolerance = %+.2f
  FormatSpecUnderTolerance = %+.2f
  Inverted = false
  LockPosition = false
  MeasureType = 1
  OverTolerance = 0
  References2D = -> [View]
  Rotation = 0
  ScaleType = 0
  TheoreticalExact = false
  Type = 2
  UnderTolerance = 0
  X = 114.324
  Y = -7.70764
FEATURE [TechDraw::DrawViewDimension] Dimension080
  Arbitrary = false
  ArbitraryTolerances = false
  EqualTolerance = true
  FormatSpec = %.2f
  FormatSpecOverTolerance = %+.2f
  FormatSpecUnderTolerance = %+.2f
  Inverted = false
  LockPosition = false
  MeasureType = 1
  OverTolerance = 0
  References2D = -> [View]
  Rotation = 0
  ScaleType = 0
  TheoreticalExact = false
  Type = 2
  UnderTolerance = 0
  X = 100.491
  Y = 64.3771
FEATURE [TechDraw::DrawViewDimension] Dimension081
  Arbitrary = false
  ArbitraryTolerances = false
  EqualTolerance = true
  FormatSpec = %.2f
  FormatSpecOverTolerance = %+.2f
  FormatSpecUnderTolerance = %+.2f
  Inverted = false
  LockPosition = false
  MeasureType = 1
  OverTolerance = 0
  References2D = -> [View]
  Rotation = 0
  ScaleType = 0
  TheoreticalExact = false
  Type = 1
  UnderTolerance = 0
  X = 70.3844
  Y = 106.526
FEATURE [TechDraw::DrawViewDimension] Dimension082
  Arbitrary = false
  ArbitraryTolerances = false
  EqualTolerance = true
  FormatSpec = %.2f
  FormatSpecOverTolerance = %+.2f
  FormatSpecUnderTolerance = %+.2f
  Inverted = false
  LockPosition = false
  MeasureType = 1
  OverTolerance = 0
  References2D = -> [View]
  Rotation = 0
  ScaleType = 0
  TheoreticalExact = false
  Type = 1
  UnderTolerance = 0
  X = -52.6468
  Y = 106.099
FEATURE [TechDraw::DrawViewDimension] Dimension083
  Arbitrary = false
  ArbitraryTolerances = false
  EqualTolerance = true
  FormatSpec = %.2f
  FormatSpecOverTolerance = %+.2f
  FormatSpecUnderTolerance = %+.2f
  Inverted = false
  LockPosition = false
  MeasureType = 1
  OverTolerance = 0
  References2D = -> [View]
  Rotation = 0
  ScaleType = 0
  TheoreticalExact = false
  Type = 2
  UnderTolerance = 0
  X = -103.645
  Y = 85.1342
FEATURE [TechDraw::DrawViewDimension] Dimension084
  Arbitrary = false
  ArbitraryTolerances = false
  EqualTolerance = true
  FormatSpec = %.2f
  FormatSpecOverTolerance = %+.2f
  FormatSpecUnderTolerance = %+.2f
  Inverted = false
  LockPosition = false
  MeasureType = 1
  OverTolerance = 0
  References2D = -> [View]
  Rotation = 0
  ScaleType = 0
  TheoreticalExact = false
  Type = 1
  UnderTolerance = 0
  X = 4.10024
  Y = -109.971
FEATURE [TechDraw::DrawViewDimension] Dimension085
  Arbitrary = false
  ArbitraryTolerances = false
  EqualTolerance = true
  FormatSpec = %.2f
  FormatSpecOverTolerance = %+.2f
  FormatSpecUnderTolerance = %+.2f
  Inverted = false
  LockPosition = false
  MeasureType = 1
  OverTolerance = 0
  References2D = -> [View]
  Rotation = 0
  ScaleType = 0
  TheoreticalExact = false
  Type = 1
  UnderTolerance = 0
  X = -49.4652
  Y = -96.9568
FEATURE [TechDraw::DrawViewDimension] Dimension086
  Arbitrary = false
  ArbitraryTolerances = false
  EqualTolerance = true
  FormatSpec = %.2f
  FormatSpecOverTolerance = %+.2f
  FormatSpecUnderTolerance = %+.2f
  Inverted = false
  LockPosition = false
  MeasureType = 1
  OverTolerance = 0
  References2D = -> [View]
  Rotation = 0
  ScaleType = 0
  TheoreticalExact = false
  Type = 1
  UnderTolerance = 0
  X = 0.891357
  Y = -97.1351
FEATURE [TechDraw::DrawViewBalloon] Balloon
  BubbleShape = 0
  EndType = 0
  EndTypeScale = 1
  KinkLength = 5
  LockPosition = false
  OriginX = 1.12575
  OriginY = 92.0033
  Rotation = 0
  ScaleType = 0
  ShapeScale = 1
  SourceView = -> View
  Text = Cable
  TextWrapLen = -1
  X = 16.8472
  Y = 104.516
FEATURE [TechDraw::DrawSVGTemplate] Template001
  EditableTexts = APPROVER_NAME=CB; AUTHOR_NAME=SnakeOil XY; DATE=2021-11-11; DN=DN; DOCUMENT_TYPE=Mechanical assembly drawing; OWNER_NAME=SnakeOil XY; PM=Silicon heater; PN=SO-250Heater; REVISION=REV B; RIGHTS=(R) DO NOT DUPLICATE THIS DRAWING TO THIRD PARTIES WITHOUT OWNER'S PERMISSION!; SCALE=0.75; SHEET=99 of 99; SIZE=A3; TITLELINE-1=SnakeOil XY; TITLELINE-2=240x230mm Silicon heater 120V 500-600W; TITLELINE-3=Dimensions in mm; TOLERANCE=+/- 0.2mm
  Height = 297
  Orientation = 1
  Width = 420
FEATURE [TechDraw::DrawViewPart] View004
  CoarseView = false
  Direction = (0,0,1)
  Focus = 100
  HardHidden = false
  IsoCount = 0
  IsoHidden = false
  IsoVisible = false
  LockPosition = false
  Perspective = false
  Rotation = 0
  Scale = 0.75
  ScaleType = 0
  SeamHidden = false
  SeamVisible = true
  SmoothHidden = false
  SmoothVisible = true
  Source = -> [Body003]
  X = 156.697
  XDirection = (1,0,0)
  Y = 159.196
FEATURE [TechDraw::DrawViewDimension] Dimension087
  Arbitrary = false
  ArbitraryTolerances = false
  EqualTolerance = true
  FormatSpec = %.2f
  FormatSpecOverTolerance = %+.2f
  FormatSpecUnderTolerance = %+.2f
  Inverted = false
  LockPosition = false
  MeasureType = 1
  OverTolerance = 0
  References2D = -> [View004]
  Rotation = 0
  ScaleType = 0
  TheoreticalExact = false
  Type = 1
  UnderTolerance = 0
  X = 0.488216
  Y = -98.2148
FEATURE [TechDraw::DrawViewDimension] Dimension088
  Arbitrary = false
  ArbitraryTolerances = false
  EqualTolerance = true
  FormatSpec = %.2f
  FormatSpecOverTolerance = %+.2f
  FormatSpecUnderTolerance = %+.2f
  Inverted = false
  LockPosition = false
  MeasureType = 1
  OverTolerance = 0
  References2D = -> [View004]
  Rotation = 0
  ScaleType = 0
  TheoreticalExact = false
  Type = 1
  UnderTolerance = 0
  X = -49.401
  Y = -90.7288
FEATURE [TechDraw::DrawViewDimension] Dimension089
  Arbitrary = false
  ArbitraryTolerances = false
  EqualTolerance = true
  FormatSpec = %.2f
  FormatSpecOverTolerance = %+.2f
  FormatSpecUnderTolerance = %+.2f
  Inverted = false
  LockPosition = false
  MeasureType = 1
  OverTolerance = 0
  References2D = -> [View004]
  Rotation = 0
  ScaleType = 0
  TheoreticalExact = false
  Type = 1
  UnderTolerance = 0
  X = -0.488216
  Y = -90.5661
FEATURE [TechDraw::DrawViewDimension] Dimension090
  Arbitrary = false
  ArbitraryTolerances = false
  EqualTolerance = true
  FormatSpec = %.2f
  FormatSpecOverTolerance = %+.2f
  FormatSpecUnderTolerance = %+.2f
  Inverted = false
  LockPosition = false
  MeasureType = 1
  OverTolerance = 0
  References2D = -> [View004]
  Rotation = 0
  ScaleType = 0
  TheoreticalExact = false
  Type = 2
  UnderTolerance = 0
  X = 94.5357
  Y = 64.429
FEATURE [TechDraw::DrawViewDimension] Dimension091
  Arbitrary = false
  ArbitraryTolerances = false
  EqualTolerance = true
  FormatSpec = %.2f
  FormatSpecOverTolerance = %+.2f
  FormatSpecUnderTolerance = %+.2f
  Inverted = false
  LockPosition = false
  MeasureType = 1
  OverTolerance = 0
  References2D = -> [View004]
  Rotation = 0
  ScaleType = 0
  TheoreticalExact = false
  Type = 2
  UnderTolerance = 0
  X = 106.741
  Y = -3.50239
FEATURE [TechDraw::DrawViewDimension] Dimension092
  Arbitrary = false
  ArbitraryTolerances = false
  EqualTolerance = true
  FormatSpec = %.2f
  FormatSpecOverTolerance = %+.2f
  FormatSpecUnderTolerance = %+.2f
  Inverted = false
  LockPosition = false
  MeasureType = 1
  OverTolerance = 0
  References2D = -> [View004]
  Rotation = 0
  ScaleType = 0
  TheoreticalExact = false
  Type = 1
  UnderTolerance = 0
  X = 78.75
  Y = 98.4414
FEATURE [TechDraw::DrawViewDimension] Dimension093
  Arbitrary = false
  ArbitraryTolerances = false
  EqualTolerance = true
  FormatSpec = %.2f
  FormatSpecOverTolerance = %+.2f
  FormatSpecUnderTolerance = %+.2f
  Inverted = false
  LockPosition = false
  MeasureType = 1
  OverTolerance = 0
  References2D = -> [View004]
  Rotation = 0
  ScaleType = 0
  TheoreticalExact = false
  Type = 1
  UnderTolerance = 0
  X = -69.7005
  Y = 97.6277
FEATURE [TechDraw::DrawViewDimension] Dimension094
  Arbitrary = false
  ArbitraryTolerances = false
  EqualTolerance = true
  FormatSpec = %.2f
  FormatSpecOverTolerance = %+.2f
  FormatSpecUnderTolerance = %+.2f
  Inverted = false
  LockPosition = false
  MeasureType = 1
  OverTolerance = 0
  References2D = -> [View004]
  Rotation = 0
  ScaleType = 0
  TheoreticalExact = false
  Type = 2
  UnderTolerance = 0
  X = -109.409
  Y = 80.7029
FEATURE [TechDraw::DrawViewBalloon] Balloon001
  BubbleShape = 0
  EndType = 0
  EndTypeScale = 1
  KinkLength = 5
  LockPosition = false
  OriginX = 1.66782
  OriginY = 117.12
  Rotation = 0
  ScaleType = 0
  ShapeScale = 1
  SourceView = -> View004
  Text = Cable
  TextWrapLen = -1
  X = 28.3345
  Y = 143.952
FEATURE [TechDraw::DrawViewAnnotation] Annotation004
  Font = osifont
  LineSpace = 80
  LockPosition = false
  MaxWidth = -1
  Rotation = 0
  ScaleType = 0
  Text = 120V 500W or over
  TextSize = 10
  TextStyle = 0
  X = 318.745
  Y = 84.3223
FEATURE [TechDraw::DrawViewAnnotation] Annotation005
  Font = osifont
  LineSpace = 80
  LockPosition = false
  MaxWidth = -1
  Rotation = 0
  ScaleType = 0
  Text = 120V 350W or over
  TextSize = 10
  TextStyle = 0
  X = 321.241
  Y = 87.7451
FEATURE [TechDraw::DrawViewDimension] Dimension095
  Arbitrary = false
  ArbitraryTolerances = false
  EqualTolerance = true
  FormatSpec = %.2f
  FormatSpecOverTolerance = %+.2f
  FormatSpecUnderTolerance = %+.2f
  Inverted = false
  LockPosition = false
  MeasureType = 1
  OverTolerance = 0
  References2D = -> [View004]
  Rotation = 0
  ScaleType = 0
  TheoreticalExact = false
  Type = 2
  UnderTolerance = 0
  X = 96.0414
  Y = -67.7926
FEATURE [TechDraw::DrawViewDimension] Dimension096
  Arbitrary = false
  ArbitraryTolerances = false
  EqualTolerance = true
  FormatSpec = %.2f
  FormatSpecOverTolerance = %+.2f
  FormatSpecUnderTolerance = %+.2f
  Inverted = false
  LockPosition = false
  MeasureType = 1
  OverTolerance = 0
  References2D = -> [View]
  Rotation = 0
  ScaleType = 0
  TheoreticalExact = false
  Type = 2
  UnderTolerance = 0
  X = 100.384
  Y = -65.2119
FEATURE [TechDraw::DrawViewAnnotation] Annotation006
  Font = osifont
  LineSpace = 80
  LockPosition = false
  MaxWidth = -1
  Rotation = 0
  ScaleType = 0
  Text = Top view (face WITHOUT adhesive)
  TextSize = 9
  TextStyle = 0
  X = 154.727
  Y = 29.1616
FEATURE [TechDraw::DrawPage] Page  label="180-heater-drawing"
  KeepUpdated = true
  NextBalloonIndex = 3
  ProjectionType = 0
  Template = -> Template
  Views = -> [View,Dimension,Dimension080,Dimension081,Dimension082,Dimension083,Dimension084,Dimension085,Dimension086,Balloon,Annotation005,Dimension096,Annotation006]
FEATURE [TechDraw::DrawViewAnnotation] Annotation007
  Font = osifont
  LineSpace = 80
  LockPosition = false
  MaxWidth = -1
  Rotation = 0
  ScaleType = 0
  Text = Top view (face WITHOUT adhesive)
  TextSize = 10
  TextStyle = 0
  X = 154.369
  Y = 32.5713
FEATURE [TechDraw::DrawPage] Page001  label="250-heater-drawing"
  KeepUpdated = true
  NextBalloonIndex = 3
  ProjectionType = 0
  Template = -> Template001
  Views = -> [View004,Dimension087,Dimension088,Dimension089,Dimension090,Dimension091,Dimension092,Dimension093,Dimension094,Balloon001,Annotation004,Dimension095,Annotation007]
FEATURE [Sketcher::SketchObject] Sketch013
  FullyConstrained = true
  MapMode = 5
  Support = -> [XY_Plane006]
  sketch-geometry (6):
    g0: LineSegment StartX=-110 StartY=100 StartZ=0 EndX=110 EndY=100 EndZ=0
    g1: LineSegment StartX=110 StartY=100 StartZ=0 EndX=110 EndY=-95 EndZ=0
    g2: LineSegment StartX=110 StartY=-95 StartZ=0 EndX=-110 EndY=-95 EndZ=0
    g3: LineSegment StartX=-110 StartY=-95 StartZ=0 EndX=-110 EndY=100 EndZ=0
    g4: Circle CenterX=-50 CenterY=95 CenterZ=0 NormalX=0 NormalY=0 NormalZ=1 AngleXU=0 Radius=2
    g5: Circle CenterX=50 CenterY=95 CenterZ=0 NormalX=0 NormalY=0 NormalZ=1 AngleXU=0 Radius=2
  constraints (18):
    c: Coincident(g0,g1)
    c: Coincident(g1,g2)
    c: Coincident(g2,g3)
    c: Coincident(g3,g0)
    c: Horizontal(g0)
    c: Horizontal(g2)
    c: Vertical(g1)
    c: Vertical(g3)
    c: DistanceX(g2,g2) = 220
    c: DistanceX(g2,g-1) = 110
    c: DistanceY(g2,g-1) = 95
    c: DistanceY(g3,g3) = 195
    c: Radius(g4) = 2
    c: Radius(g5) = 2
    c: DistanceY(g4,g0) = 5
    c: DistanceY(g5,g0) = 5
    c: DistanceX(g4,g-1) = 50
    c: DistanceX(g-1,g5) = 50
FEATURE [PartDesign::Pad] Pad011
  Direction = (1,1,1)
  Length = 3
  Length2 = 100
  Profile = -> Sketch013
  Type = 0
FEATURE [PartDesign::Chamfer] Chamfer
  Angle = 45
  Base = -> Pad011 [Edge1,Edge8,Edge2,Edge5]
  BaseFeature = -> Pad011
  ChamferType = 0
  FlipDirection = false
  Size = 3
  Size2 = 1
  SupportTransform = false
FEATURE [PartDesign::Body] Body004  label="190-glass"
  Group = -> [Sketch013,Pad011,Chamfer]
  Origin = -> Origin006
  Tip = -> Chamfer
FEATURE [Sketcher::SketchObject] Sketch014
  FullyConstrained = true
  MapMode = 5
  Support = -> [XY_Plane007]
  sketch-geometry (6):
    g0: LineSegment StartX=-140 StartY=123 StartZ=0 EndX=140 EndY=123 EndZ=0
    g1: LineSegment StartX=140 StartY=123 StartZ=0 EndX=140 EndY=-117 EndZ=0
    g2: LineSegment StartX=140 StartY=-117 StartZ=0 EndX=-140 EndY=-117 EndZ=0
    g3: LineSegment StartX=-140 StartY=-117 StartZ=0 EndX=-140 EndY=123 EndZ=0
    g4: Circle CenterX=-70 CenterY=118 CenterZ=0 NormalX=0 NormalY=0 NormalZ=1 AngleXU=0 Radius=2
    g5: Circle CenterX=70 CenterY=118 CenterZ=0 NormalX=0 NormalY=0 NormalZ=1 AngleXU=0 Radius=2
  constraints (18):
    c: Coincident(g0,g1)
    c: Coincident(g1,g2)
    c: Coincident(g2,g3)
    c: Coincident(g3,g0)
    c: Horizontal(g0)
    c: Horizontal(g2)
    c: Vertical(g1)
    c: Vertical(g3)
    c: DistanceX(g2,g2) = 280
    c: DistanceX(g2,g-1) = 140
    c: DistanceY(g2,g-1) = 117
    c: DistanceY(g3,g3) = 240
    c: DistanceY(g5,g4) = 0
    c: DistanceX(g4,g5) = 140
    c: DistanceX(g4,g-1) = 70
    c: Radius(g4) = 2
    c: Radius(g5) = 2
    c: DistanceY(g4,g0) = 5
FEATURE [PartDesign::Pad] Pad012
  Direction = (1,1,1)
  Length = 3
  Length2 = 100
  Profile = -> Sketch014
  Type = 0
FEATURE [PartDesign::Chamfer] Chamfer001
  Angle = 45
  Base = -> Pad012 [Edge5,Edge2,Edge8,Edge1]
  BaseFeature = -> Pad012
  ChamferType = 0
  FlipDirection = false
  Size = 3
  Size2 = 1
  SupportTransform = false
FEATURE [PartDesign::Body] Body005  label="250-glass"
  Group = -> [Sketch014,Pad012,Chamfer001]
  Origin = -> Origin007
  Tip = -> Chamfer001
FEATURE [TechDraw::DrawSVGTemplate] Template004
  EditableTexts = AuthorName=SnakeOil XY; CheckDate=2021-11-15; CreationDate=2021-11-15; DrawingNumber=1; FC-Scale=0.75; FC-Title=Glass bed plate (280x240mm); SheetNumber=1 of 1; Subtitle=for 250 machine; SupervisorName=SnakeOil XY; Weight=-
  Height = 297
  Orientation = 1
  Width = 420
FEATURE [TechDraw::DrawViewPart] View005
  CoarseView = false
  Direction = (0,0,1)
  Focus = 100
  HardHidden = false
  IsoCount = 0
  IsoHidden = false
  IsoVisible = false
  LockPosition = false
  Perspective = false
  Rotation = 0
  Scale = 0.75
  ScaleType = 0
  SeamHidden = false
  SeamVisible = true
  SmoothHidden = false
  SmoothVisible = true
  Source = -> [Body005]
  X = 140.514
  XDirection = (1,0,0)
  Y = 176.364
FEATURE [TechDraw::DrawViewDimension] Dimension097
  Arbitrary = false
  ArbitraryTolerances = false
  EqualTolerance = true
  FormatSpec = %.2f
  FormatSpecOverTolerance = %+.2f
  FormatSpecUnderTolerance = %+.2f
  Inverted = false
  LockPosition = false
  MeasureType = 1
  OverTolerance = 0
  References2D = -> [View005]
  Rotation = 0
  ScaleType = 0
  TheoreticalExact = false
  Type = 1
  UnderTolerance = 0
  X = -0.540951
  Y = -95.0058
FEATURE [TechDraw::DrawViewDimension] Dimension098
  Arbitrary = false
  ArbitraryTolerances = false
  EqualTolerance = true
  FormatSpec = %.2f
  FormatSpecOverTolerance = %+.2f
  FormatSpecUnderTolerance = %+.2f
  Inverted = false
  LockPosition = false
  MeasureType = 1
  OverTolerance = 0
  References2D = -> [View005]
  Rotation = 0
  ScaleType = 0
  TheoreticalExact = false
  Type = 2
  UnderTolerance = 0
  X = -119.949
  Y = 0
FEATURE [TechDraw::DrawViewDimension] Dimension099
  Arbitrary = false
  ArbitraryTolerances = false
  EqualTolerance = true
  FormatSpec = %.2f
  FormatSpecOverTolerance = %+.2f
  FormatSpecUnderTolerance = %+.2f
  Inverted = false
  LockPosition = false
  MeasureType = 1
  OverTolerance = 0
  References2D = -> [View005]
  Rotation = 0
  ScaleType = 0
  TheoreticalExact = false
  Type = 1
  UnderTolerance = 0
  X = -79.3713
  Y = 103.152
FEATURE [TechDraw::DrawViewDimension] Dimension101
  Arbitrary = false
  ArbitraryTolerances = false
  EqualTolerance = true
  FormatSpec = %.2f
  FormatSpecOverTolerance = %+.2f
  FormatSpecUnderTolerance = %+.2f
  Inverted = false
  LockPosition = false
  MeasureType = 1
  OverTolerance = 0
  References2D = -> [View005]
  Rotation = 0
  ScaleType = 0
  TheoreticalExact = false
  Type = 2
  UnderTolerance = 0
  X = -112.881
  Y = 79.5828
FEATURE [TechDraw::DrawViewDimension] Dimension102
  Arbitrary = false
  ArbitraryTolerances = false
  EqualTolerance = true
  FormatSpec = 2x ⌀%.2f THRU ALL
  FormatSpecOverTolerance = %+.2f
  FormatSpecUnderTolerance = %+.2f
  Inverted = false
  LockPosition = false
  MeasureType = 1
  OverTolerance = 0
  References2D = -> [View005]
  Rotation = 0
  ScaleType = 0
  TheoreticalExact = false
  Type = 5
  UnderTolerance = 0
  X = 67.9865
  Y = 79.8688
FEATURE [TechDraw::DrawViewBalloon] Balloon002
  BubbleShape = 6
  EndType = 0
  EndTypeScale = 1
  KinkLength = 5
  LockPosition = false
  OriginX = 138.986
  OriginY = -117.295
  Rotation = 0
  ScaleType = 0
  ShapeScale = 1
  SourceView = -> View005
  Text = 4x 3mm chamfer or fillet
  TextWrapLen = -1
  X = 190.129
  Y = -99.0812
FEATURE [TechDraw::DrawViewDimension] Dimension103
  Arbitrary = false
  ArbitraryTolerances = false
  EqualTolerance = true
  FormatSpec = %.2f
  FormatSpecOverTolerance = %+.2f
  FormatSpecUnderTolerance = %+.2f
  Inverted = false
  LockPosition = false
  MeasureType = 1
  OverTolerance = 0
  References2D = -> [View005]
  Rotation = 0
  ScaleType = 0
  TheoreticalExact = false
  Type = 1
  UnderTolerance = 0
  X = -29.4304
  Y = 103.1
FEATURE [TechDraw::DrawViewAnnotation] Annotation008
  Font = osifont
  LineSpace = 80
  LockPosition = false
  MaxWidth = -1
  Rotation = 0
  ScaleType = 0
  Text = Dimensions in mm
  TextSize = 5
  TextStyle = 0
  X = 287.05
  Y = 31.8661
FEATURE [TechDraw::DrawPage] Page004  label="250-glass-drawing"
  KeepUpdated = true
  NextBalloonIndex = 2
  ProjectionType = 0
  Template = -> Template004
  Views = -> [View005,Dimension097,Dimension098,Dimension099,Dimension101,Dimension102,Balloon002,Dimension103,Annotation008]
note: 2 file-system paths scrubbed to <path> (originals preserved in the JSON sidecar)
